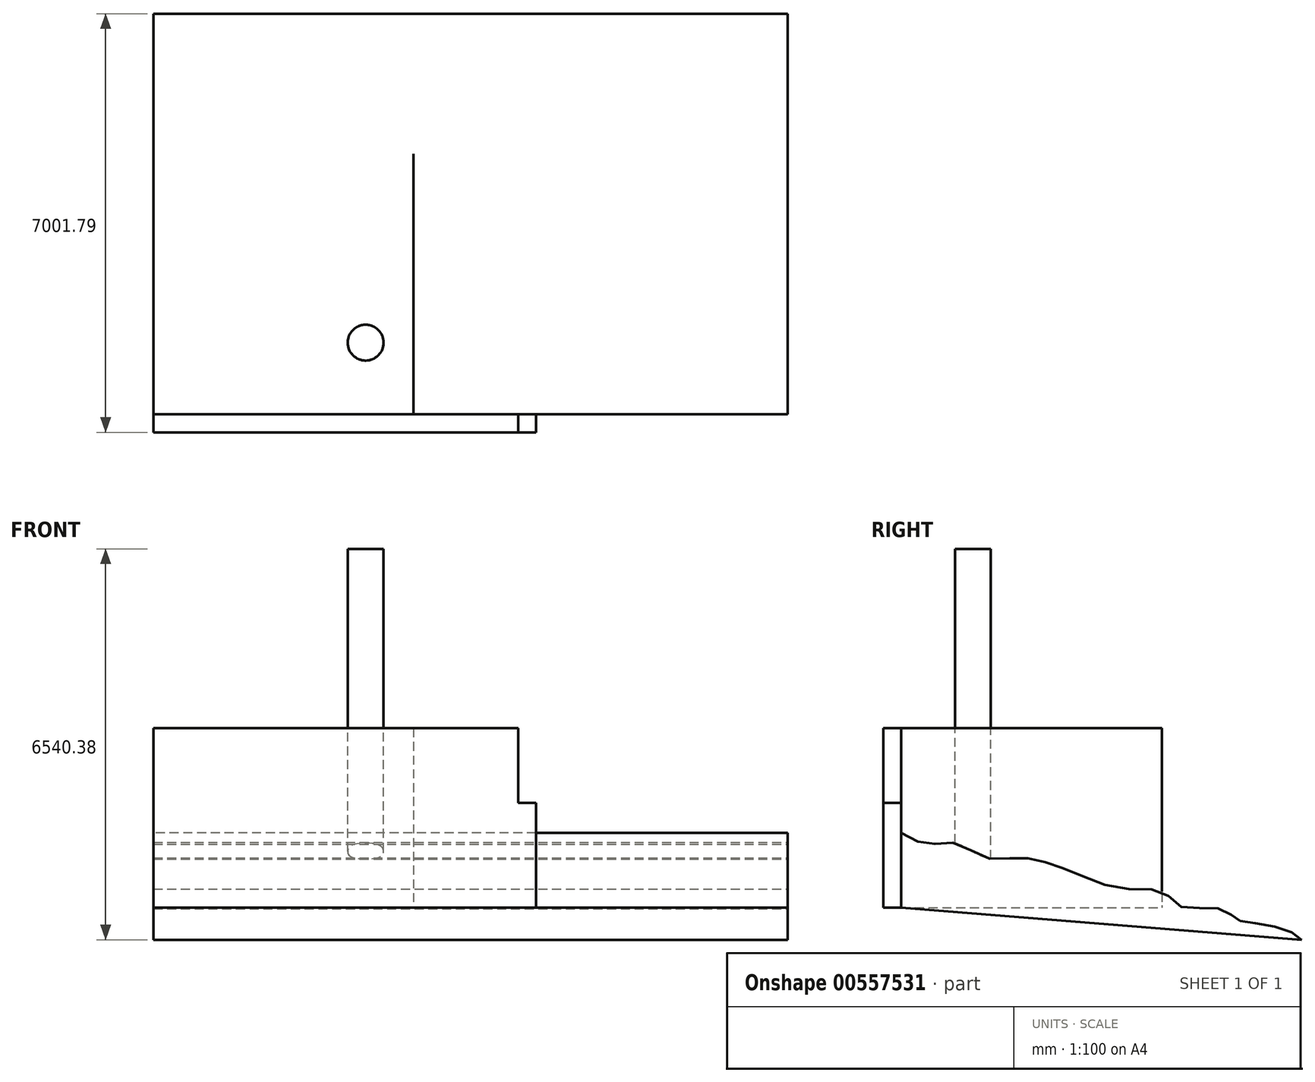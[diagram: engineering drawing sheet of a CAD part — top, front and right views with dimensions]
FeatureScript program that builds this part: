
annotation { "Feature Type Name" : "Feature", "Feature Type Description" : "" }
export const myFeature = defineFeature(function(context is Context, id is Id, definition is map)
    precondition{}
    {
        {
            var Q0;
            Q0=qCreatedBy(makeId("Top.planeOp"),FACE);
            var sketch = newSketch(context, id + "F0", { "sketchPlane" : qUnion([Q0])});
            skLineSegment(sketch, "E0.bottom", {"start": v(0, 0) * mm, "end": v(5800, 0) * mm});
            skLineSegment(sketch, "E0.top", {"start": v(0, -300) * mm, "end": v(5800, -300) * mm});
            skLineSegment(sketch, "E0.left", {"start": v(0, 0) * mm, "end": v(0, -300) * mm});
            skLineSegment(sketch, "E0.right", {"start": v(5800, 0) * mm, "end": v(5800, -300) * mm});
            skSolve(sketch);
        }
        {
            var Q0;
            Q0=makeQuery(id+"F0.imprint","IMPRINT",FACE,{"disambiguationData":[TD([[makeQuery(id+"F0.imprint","IMPRINT",EDGE,{"derivedFrom":sQuery(id+"F0.wireOp",EDGE,"E0.bottom")}),-1.0]])]});
            extrude(context, id + "F1", {"entities" : qUnion([Q0]), "depth" : 3000 * mm, "offsetDistance" : 25 * mm});
        }
        {
            var Q0;
            Q0=makeQuery(id+"F1.opExtrude","SWEPT_FACE",FACE,{"disambiguationData":[OSD([sQuery(id+"F0.wireOp",EDGE,"E0.right")])]});
            var sketch = newSketch(context, id + "F2", { "sketchPlane" : qUnion([Q0])});
            skLineSegment(sketch, "E1.bottom", {"start": v(-300, 0) * mm, "end": v(0, 0) * mm});
            skLineSegment(sketch, "E1.top", {"start": v(-300, 1750) * mm, "end": v(0, 1750) * mm});
            skLineSegment(sketch, "E1.left", {"start": v(-300, 0) * mm, "end": v(-300, 1750) * mm});
            skLineSegment(sketch, "E1.right", {"start": v(0, 0) * mm, "end": v(0, 1750) * mm});
            skSolve(sketch);
        }
        {
            var Q0;
            Q0=makeQuery(id+"F2.imprint","IMPRINT",FACE,{"disambiguationData":[TD([[makeQuery(id+"F2.imprint","IMPRINT",EDGE,{"derivedFrom":sQuery(id+"F2.wireOp",EDGE,"E1.bottom")}),-1.0]])]});
            extrude(context, id + "F3", {"entities" : qUnion([Q0]), "operationType" : NewBodyOperationType.ADD, "depth" : 300 * mm, "offsetDistance" : 25 * mm});
        }
        {
            var Q0;
            Q0=makeQuery(id+"F1.opExtrude","SWEPT_FACE",FACE,{"disambiguationData":[OSD([sQuery(id+"F0.wireOp",EDGE,"E0.left")])]});
            var sketch = newSketch(context, id + "F4", { "sketchPlane" : qUnion([Q0])});
            skLineSegment(sketch, "E2.bottom", {"start": v(0, 0) * mm, "end": v(300, 0) * mm});
            skLineSegment(sketch, "E2.top", {"start": v(0, 1960) * mm, "end": v(300, 1960) * mm});
            skLineSegment(sketch, "E2.left", {"start": v(0, 0) * mm, "end": v(0, 1960) * mm});
            skLineSegment(sketch, "E2.right", {"start": v(300, 0) * mm, "end": v(300, 1960) * mm});
            skSolve(sketch);
        }
        {
            var Q0;
            Q0=makeQuery(id+"F4.imprint","IMPRINT",FACE,{"disambiguationData":[TD([[makeQuery(id+"F4.imprint","IMPRINT",EDGE,{"derivedFrom":sQuery(id+"F4.wireOp",EDGE,"E2.bottom")}),1.0]])]});
            extrude(context, id + "F5", {"entities" : qUnion([Q0]), "operationType" : NewBodyOperationType.ADD, "depth" : 300 * mm, "offsetDistance" : 25 * mm});
        }
        {
            var Q0;
            Q0=makeQuery(id+"F1.opExtrude","SWEPT_FACE",FACE,{"disambiguationData":[OSD([sQuery(id+"F0.wireOp",EDGE,"E0.right")])]});
            var sketch = newSketch(context, id + "F6", { "sketchPlane" : qUnion([Q0])});
            skLineSegment(sketch, "E3.bottom", {"start": v(-300, 3000) * mm, "end": v(0, 3000) * mm});
            skLineSegment(sketch, "E3.top", {"start": v(-300, 1750) * mm, "end": v(0, 1750) * mm});
            skLineSegment(sketch, "E3.left", {"start": v(-300, 3000) * mm, "end": v(-300, 1750) * mm});
            skLineSegment(sketch, "E3.right", {"start": v(0, 3000) * mm, "end": v(0, 1750) * mm});
            skSolve(sketch);
        }
        {
            var Q0;
            Q0=makeQuery(id+"F1.opExtrude","SWEPT_FACE",FACE,{"disambiguationData":[OSD([sQuery(id+"F0.wireOp",EDGE,"E0.left")])]});
            var Q1;
            {var subQ0=sQuery(id+"F4.wireOp",EDGE,"E2.right");Q1=makeQuery(id+"Fhfy4alrJVKUPPf_1.boolean.opBoolean","MERGE",FACE,{"derivedFrom":[makeQuery(id+"F5.opExtrude","CAP_FACE",FACE,{"disambiguationData":[OSD([sQuery(id+"F4.wireOp",EDGE,"E2.bottom"),sQuery(id+"F4.wireOp",EDGE,"E2.top"),sQuery(id+"F4.wireOp",EDGE,"E2.left"),subQ0])],"isStart":false}),makeQuery(id+"Fhfy4alrJVKUPPf_1.opExtrude","SWEPT_FACE",FACE,{"disambiguationData":[OSD([subQ0])]})]});}
            extrude(context, id + "F7", {"entities" : qUnion([Q0]), "operationType" : NewBodyOperationType.ADD, "endBound" : BoundingType.UP_TO_SURFACE, "depth" : 25 * mm, "endBoundEntityFace" : qUnion([Q1]), "offsetDistance" : 25 * mm});
        }
        {
            var Q0;
            {var subQ0=sQuery(id+"F4.wireOp",EDGE,"E2.right");var subQ1=sQuery(id+"F4.wireOp",EDGE,"E2.left");var subQ2=sQuery(id+"F4.wireOp",EDGE,"E2.top");var subQ3=sQuery(id+"F4.wireOp",EDGE,"E2.bottom");Q0=makeQuery(id+"F7.boolean.opBoolean","MERGE",FACE,{"derivedFrom":[makeQuery(id+"Fhfy4alrJVKUPPf_1.boolean.opBoolean","MERGE",FACE,{"derivedFrom":[makeQuery(id+"F5.opExtrude","CAP_FACE",FACE,{"disambiguationData":[OSD([subQ3,subQ2,subQ1,subQ0])],"isStart":false}),makeQuery(id+"Fhfy4alrJVKUPPf_1.opExtrude","SWEPT_FACE",FACE,{"disambiguationData":[OSD([subQ0])]})]}),makeQuery(id+"F7.opExtrude","CAP_FACE",FACE,{"disambiguationData":[OSD([subQ3,subQ2,subQ1,subQ0])],"isStart":false})]});}
            var sketch = newSketch(context, id + "F8", { "sketchPlane" : qUnion([Q0])});
            skPoint(sketch, "E4", {"position": v(0, 1250) * mm});
            skFitSpline(sketch, "E5", {"points": [v(0, 1250) * mm, v(-437.44, 1059.03) * mm, v(-894.42, 1078.07) * mm, v(-1427.55, 830.54) * mm, v(-1979.73, 830.54) * mm, v(-2417.66, 754.38) * mm, v(-2931.76, 563.98) * mm, v(-3712.42, 316.45) * mm, v(-4378.84, 259.33) * mm, v(-4702.53, 0) * mm, v(-5216.62, 0) * mm, v(-5521.27, -121.48) * mm, v(-5654.56, -216.69) * mm, v(-6016.33, -273.8) * mm, v(-6511.38, -407.1) * mm, v(-6701.79, -540.38) * mm], "startDerivative": vector(-6309.5, -3946.15) * mm, "endDerivative": vector(-3345.26, -2921.8) * mm});
            skLineSegment(sketch, "E6", {"start": v(-6701.79, -540.38) * mm, "end": v(0, 0) * mm});
            skLineSegment(sketch, "E7", {"start": v(0, 0) * mm, "end": v(0, 1250) * mm});
            skSolve(sketch);
        }
        {
            var Q0;
            {var subQ0=sQuery(id+"F0.wireOp",EDGE,"E0.bottom");Q0=makeQuery(id+"F7.boolean.opBoolean","MERGE",FACE,{"derivedFrom":[makeQuery(id+"FmAnOcS3EmCuHOY_1.boolean.opBoolean","MERGE",FACE,{"derivedFrom":[makeQuery(id+"F5.boolean.opBoolean","MERGE",FACE,{"derivedFrom":[makeQuery(id+"F3.boolean.opBoolean","MERGE",FACE,{"derivedFrom":[makeQuery(id+"F1.opExtrude","SWEPT_FACE",FACE,{"disambiguationData":[OSD([subQ0])]}),makeQuery(id+"F3.opExtrude","SWEPT_FACE",FACE,{"disambiguationData":[OSD([sQuery(id+"F2.wireOp",EDGE,"E1.right")])]})]}),makeQuery(id+"F5.opExtrude","SWEPT_FACE",FACE,{"disambiguationData":[OSD([sQuery(id+"F4.wireOp",EDGE,"E2.left")])]})]}),makeQuery(id+"FmAnOcS3EmCuHOY_1.opExtrude","SWEPT_FACE",FACE,{"disambiguationData":[OSD([sQuery(id+"F6.wireOp",EDGE,"E3.right")])]})]}),makeQuery(id+"F7.opExtrude","SWEPT_FACE",FACE,{"disambiguationData":[OSD([subQ0,sQuery(id+"F0.wireOp",EDGE,"E0.left")])]})]});}
            var sketch = newSketch(context, id + "F9", { "sketchPlane" : qUnion([Q0])});
            skLineSegment(sketch, "E8", {"start": v(-4050, 3000) * mm, "end": v(-4050, 0) * mm});
            skSolve(sketch);
        }
        {
            var Q0;
            Q0=sQuery(id+"F9.wireOp",EDGE,"E8");
            extrude(context, id + "F10", {"bodyType" : ToolBodyType.SURFACE, "surfaceEntities" : qUnion([Q0]), "depth" : 4360 * mm, "offsetDistance" : 25 * mm});
        }
        {
            var Q0;
            {var subQ0=sQuery(id+"F0.wireOp",EDGE,"E0.left");Q0=makeQuery(id+"F7.boolean.opBoolean","MERGE",FACE,{"derivedFrom":[makeQuery(id+"FmAnOcS3EmCuHOY_1.boolean.opBoolean","MERGE",FACE,{"derivedFrom":[makeQuery(id+"F1.opExtrude","CAP_FACE",FACE,{"disambiguationData":[OSD([sQuery(id+"F0.wireOp",EDGE,"E0.bottom"),sQuery(id+"F0.wireOp",EDGE,"E0.top"),subQ0,sQuery(id+"F0.wireOp",EDGE,"E0.right")])],"isStart":false}),makeQuery(id+"FmAnOcS3EmCuHOY_1.opExtrude","SWEPT_FACE",FACE,{"disambiguationData":[OSD([sQuery(id+"F6.wireOp",EDGE,"E3.bottom")])]})]}),makeQuery(id+"F7.opExtrude","SWEPT_FACE",FACE,{"disambiguationData":[OSD([subQ0])]})]});}
            var sketch = newSketch(context, id + "F11", { "sketchPlane" : qUnion([Q0])});
            skCircle(sketch, "E9", {"center": v(3250, 1200) * mm, "radius": 300 * mm});
            skSolve(sketch);
        }
        {
            var Q0;
            Q0 = qSketchRegion(id + "F8", true);
            extrude(context, id + "F12", {"entities" : qUnion([Q0]), "oppositeDirection" : true, "depth" : 10610 * mm, "offsetDistance" : 25 * mm});
        }
        {
            var Q0;
            Q0=makeQuery(id+"F11.imprint","IMPRINT",FACE,{"disambiguationData":[TD([[makeQuery(id+"F11.imprint","IMPRINT",EDGE,{"derivedFrom":sQuery(id+"F11.wireOp",EDGE,"E9")}),1.0]])]});
            var Q1;
            Q1=makeQuery(id+"F12.opExtrude","SWEPT_FACE",FACE,{"disambiguationData":[OSD([sQuery(id+"F8.wireOp",EDGE,"E5")])]});
            extrude(context, id + "F13", {"entities" : qUnion([Q0]), "operationType" : NewBodyOperationType.ADD, "endBound" : BoundingType.UP_TO_SURFACE, "oppositeDirection" : true, "depth" : 25 * mm, "endBoundEntityFace" : qUnion([Q1]), "offsetDistance" : 25 * mm});
        }
        {
            var Q0;
            Q0=makeQuery(id+"F13.opExtrude","CAP_FACE",FACE,{"disambiguationData":[OSD([sQuery(id+"F11.wireOp",EDGE,"E9")])],"isStart":true});
            extrude(context, id + "F14", {"entities" : qUnion([Q0]), "operationType" : NewBodyOperationType.ADD, "depth" : 3000 * mm, "offsetDistance" : 25 * mm});
        }
        {
            var Q0;
            Q0=makeQuery(id+"F10.opExtrude","SWEPT_FACE",FACE,{"disambiguationData":[OSD([sQuery(id+"F9.wireOp",EDGE,"E8")])]});
            extrude(context, id + "F15", {"entities" : qUnion([Q0]), "depth" : 1 * mm, "offsetDistance" : 25 * mm});
        }
        {
            var Q0;
            Q0=makeQuery(id+"F5.boolean.opBoolean","MERGE",FACE,{"derivedFrom":[makeQuery(id+"F3.boolean.opBoolean","MERGE",FACE,{"derivedFrom":[makeQuery(id+"F1.opExtrude","CAP_FACE",FACE,{"disambiguationData":[OSD([sQuery(id+"F0.wireOp",EDGE,"E0.bottom"),sQuery(id+"F0.wireOp",EDGE,"E0.top"),sQuery(id+"F0.wireOp",EDGE,"E0.left"),sQuery(id+"F0.wireOp",EDGE,"E0.right")])],"isStart":true}),makeQuery(id+"F3.opExtrude","SWEPT_FACE",FACE,{"disambiguationData":[OSD([sQuery(id+"F2.wireOp",EDGE,"E1.bottom")])]})]}),makeQuery(id+"F5.opExtrude","SWEPT_FACE",FACE,{"disambiguationData":[OSD([sQuery(id+"F4.wireOp",EDGE,"E2.bottom")])]})]});
            cPlane(context, id + "F16", {"entities" : qUnion([Q0]), "cplaneType" : CPlaneType.OFFSET, "offset" : 60 * mm, "oppositeDirection" : true, "width" : 150 * mm, "height" : 150 * mm});
        }
    });
